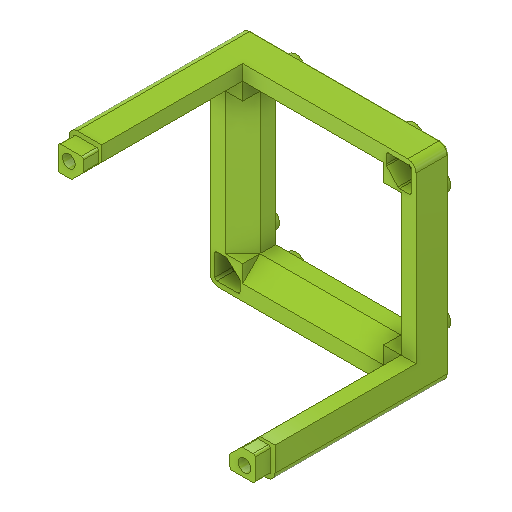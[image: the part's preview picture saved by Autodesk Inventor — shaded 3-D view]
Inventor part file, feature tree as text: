
AUTODESK INVENTOR PART (.ipt)
format: ipt  version: 2022 (Build 260153000, 153)  size: 422,912 bytes
history: native  units: mm
features: projected_geometry x11, extrude x8, sketch x7, plane x4, hole x1, fillet x1
ambient origin geometry x8: Origin, YZ Plane, XZ Plane, XY Plane, X Axis, Y Axis, Z Axis, Center Point
bodies: Solid1 (feature_tree)
feature tree (32):
  extrude  "Extrusion1"  Depth=49.8mm
  extrude  "Extrusion2"  Depth=8.0mm TaperAngle=0.0deg
  hole  "Hole1"  [1 undecoded]
  extrude  "Extrusion3"  Depth=33.8mm TaperAngle=0.0deg
  extrude  "Extrusion4"  Depth=3.65mm
  plane  "Work Plane1"
  extrude  "Extrusion5"  Depth=54.15mm
  extrude  "Extrusion7"  Depth=54.15mm
  extrude  "Extrusion8"  Depth=54.15mm
  fillet  "Fillet2"  Radius=3.65mm
  extrude  "Extrusion10"  TaperAngle=45.0deg  [1 undecoded]
  plane  "Work Plane2"
  plane  "Work Plane3"
  plane  "Work Plane4"
  sketch  "Sketch1"  dims[d0=49.8mm d1=49.8mm]
  sketch  "Sketch2"  dims[d2=7.88mm d3=8.0mm d4=0.0mm]
  projected_geometry  "Projected Loop1"
  sketch  "Sketch3"  dims[d5=34.1mm d6=0.0mm]
  sketch  "Sketch6"  dims[d8=3.1mm d9=6.0mm d10=5.5mm d11=4.6mm d12=90.0deg d13=16.0mm d14=20.594885mm d30=33.8mm d31=0.0mm]
  projected_geometry  "Projected Loop4"
  projected_geometry  "Projected Loop6"
  sketch  "Sketch7"  dims[d35=33.8mm d36=0.0mm d40=33.8mm d41=0.0mm]
  projected_geometry  "Projected Loop16"
  projected_geometry  "Projected Loop17"
  sketch  "Sketch18"  dims[d96=3.65mm d97=3.65mm]
  sketch  "Sketch20"  dims[d98=3.65mm d99=3.65mm d100=3.65mm d101=3.65mm d102=3.65mm d112=45.0deg d124=3.7mm d125=0.0mm d130=4.2mm d131=0.0mm d132=2.0mm d133=0.5mm d144=4.95mm d145=2.05mm d146=5.5mm d147=40.0mm d149=360.0deg d151=2.2mm d152=-0.349066mm d164=3.1mm d169=6.1mm d170=6.1mm d171=6.1mm d172=6.1mm d173=1.1mm d174=1.1mm d177=4.18mm d181=4.18mm d182=4.18mm d183=4.18mm d187=54.15mm d188=45.0deg d189=54.15mm d190=135.0deg d191=135.0deg d192=54.15mm d193=54.15mm d194=0.0mm d195=0.0mm]
  projected_geometry  "Projected Loop23"
  projected_geometry  "Projected Loop28"
  projected_geometry  "Projected Loop29"
  projected_geometry  "Projizierte Kontur30"
  projected_geometry  "Projizierte Kontur31"
  projected_geometry  "Projizierte Kontur32"
note: 2 required parameter values undecoded (feature->parameter linkage not recoverable at this tier; creation-order binding heuristic only, values carry confidence <= 0.55)
